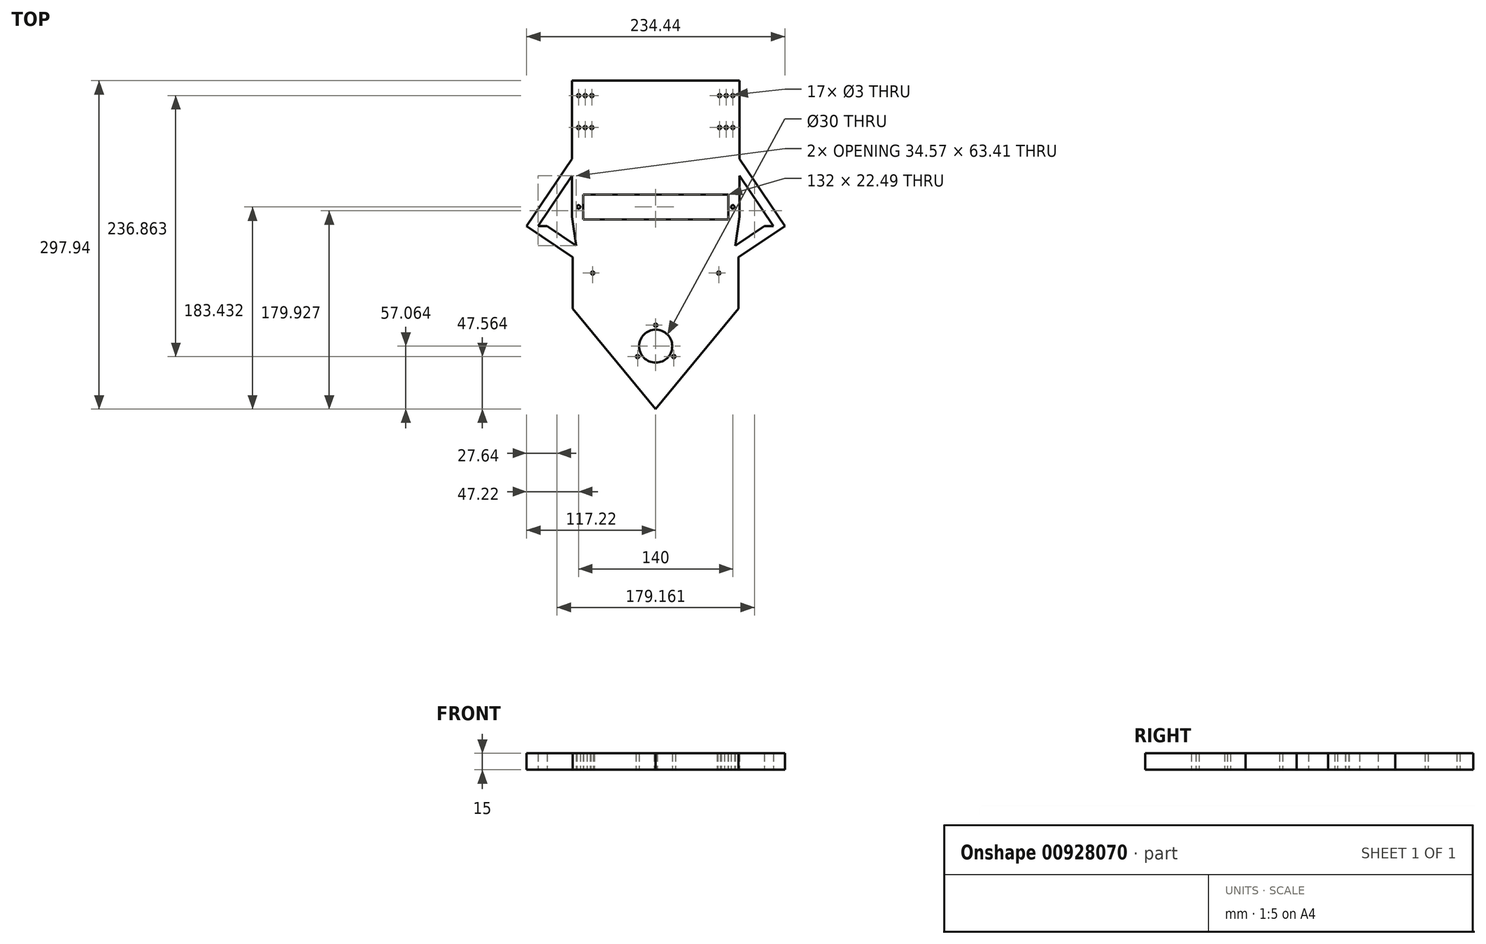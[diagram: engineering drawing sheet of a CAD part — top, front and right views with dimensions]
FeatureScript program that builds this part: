
annotation { "Feature Type Name" : "Feature", "Feature Type Description" : "" }
export const myFeature = defineFeature(function(context is Context, id is Id, definition is map)
    precondition{}
    {
        {
            var Q0;
            Q0=qCreatedBy(makeId("Top.planeOp"),FACE);
            var sketch = newSketch(context, id + "F0", { "sketchPlane" : qUnion([Q0])});
            skLineSegment(sketch, "E0.top", {"start": v(76, 131.87) * mm, "end": v(-76, 131.87) * mm});
            skLineSegment(sketch, "E0.left", {"start": v(76, 8.63) * mm, "end": v(76, 131.87) * mm});
            skLineSegment(sketch, "E0.right", {"start": v(-76, 8.63) * mm, "end": v(-76, 131.87) * mm});
            skPoint(sketch, "E0.middle", {"position": v(0, 70.25) * mm});
            skCircle(sketch, "E1", {"center": v(70, 118.36) * mm, "radius": 1.5 * mm});
            skCircle(sketch, "E2.1.0.0", {"center": v(64, 118.36) * mm, "radius": 1.5 * mm});
            skCircle(sketch, "E2.2.0.0", {"center": v(58, 118.36) * mm, "radius": 1.5 * mm});
            skCircle(sketch, "E3.MirrorC", {"center": v(58, 89.36) * mm, "radius": 1.5 * mm});
            skCircle(sketch, "E4.MirrorC", {"center": v(70, 89.36) * mm, "radius": 1.5 * mm});
            skCircle(sketch, "E5.MirrorC", {"center": v(64, 89.36) * mm, "radius": 1.5 * mm});
            skCircle(sketch, "E6.MirrorC", {"center": v(-58, 118.36) * mm, "radius": 1.5 * mm});
            skCircle(sketch, "E7.MirrorC", {"center": v(-64, 118.36) * mm, "radius": 1.5 * mm});
            skCircle(sketch, "E8.MirrorC", {"center": v(-70, 118.36) * mm, "radius": 1.5 * mm});
            skCircle(sketch, "E9.MirrorC", {"center": v(-58, 89.36) * mm, "radius": 1.5 * mm});
            skCircle(sketch, "E10.MirrorC", {"center": v(-64, 89.36) * mm, "radius": 1.5 * mm});
            skCircle(sketch, "E11.MirrorC", {"center": v(-70, 89.36) * mm, "radius": 1.5 * mm});
            skLineSegment(sketch, "E12", {"start": v(0, 74) * mm, "end": v(0, -73.54) * mm});
            skLineSegment(sketch, "E13", {"start": v(-83.19, 105.86) * mm, "end": v(-83.19, 60.86) * mm});
            skLineSegment(sketch, "E14", {"start": v(-76, 60.86) * mm, "end": v(-117.22, 0) * mm});
            skLineSegment(sketch, "E15", {"start": v(-117.22, 0) * mm, "end": v(-75.22, -28.45) * mm});
            skLineSegment(sketch, "E16", {"start": v(-76, 45.56) * mm, "end": v(-106.87, 0) * mm});
            skLineSegment(sketch, "E17", {"start": v(-104.28, 3.82) * mm, "end": v(-72.3, -17.85) * mm});
            skLineSegment(sketch, "E18", {"start": v(-75.22, -28.45) * mm, "end": v(-75.22, -75.05) * mm});
            skLineSegment(sketch, "E19", {"start": v(-58.47, -47.62) * mm, "end": v(-58.47, -45.58) * mm});
            skLineSegment(sketch, "E20", {"start": v(0, -73.54) * mm, "end": v(0, -166.07) * mm});
            skLineSegment(sketch, "E21", {"start": v(0, -166.07) * mm, "end": v(-75.22, -75.05) * mm});
            skLineSegment(sketch, "E22.MirrorCS", {"start": v(76, 60.86) * mm, "end": v(117.22, 0) * mm});
            skLineSegment(sketch, "E23.MirrorCS", {"start": v(76, 45.56) * mm, "end": v(106.87, 0) * mm});
            skLineSegment(sketch, "E24.MirrorCS", {"start": v(117.22, 0) * mm, "end": v(75.22, -28.45) * mm});
            skLineSegment(sketch, "E25.MirrorCS", {"start": v(104.28, 3.82) * mm, "end": v(72.3, -17.85) * mm});
            skLineSegment(sketch, "E26.MirrorCS", {"start": v(58.47, -47.62) * mm, "end": v(58.47, -45.58) * mm});
            skLineSegment(sketch, "E27.MirrorCS", {"start": v(75.22, -28.45) * mm, "end": v(75.22, -75.05) * mm});
            skLineSegment(sketch, "E28.MirrorCS", {"start": v(0, -166.07) * mm, "end": v(75.22, -75.05) * mm});
            skCircle(sketch, "E29", {"center": v(0, -109) * mm, "radius": 15 * mm});
            skLineSegment(sketch, "E30", {"start": v(117.22, 0) * mm, "end": v(-117.22, 0) * mm});
            skLineSegment(sketch, "E31", {"start": v(87.88, 28.02) * mm, "end": v(83.88, 28.02) * mm});
            skPoint(sketch, "E32.end.orphan", {"position": v(-58.47, -75.05) * mm});
            skPoint(sketch, "E33.MirrorCS.end.orphan", {"position": v(58.47, -75.05) * mm});
            skPoint(sketch, "E33.MirrorCS.start.orphan", {"position": v(75.22, -75.05) * mm});
            skPoint(sketch, "E34.orphan", {"position": v(-64.47, -23.15) * mm});
            skPoint(sketch, "E35.orphan", {"position": v(-83.05, -23.15) * mm});
            skPoint(sketch, "E36.orphan", {"position": v(75.22, -28.45) * mm});
            skPoint(sketch, "E37.orphan", {"position": v(83.05, -23.15) * mm});
            skPoint(sketch, "E38.orphan", {"position": v(111.38, 8.63) * mm});
            skPoint(sketch, "E39.orphan", {"position": v(110.12, -4.81) * mm});
            skPoint(sketch, "E40.orphan", {"position": v(-110.12, -4.81) * mm});
            skPoint(sketch, "E41.orphan", {"position": v(-111.38, 8.63) * mm});
            skPoint(sketch, "E42.orphan", {"position": v(-65.64, 60.86) * mm});
            skPoint(sketch, "E43.orphan", {"position": v(65.64, 60.86) * mm});
            skPoint(sketch, "E44.orphan", {"position": v(64.47, -23.15) * mm});
            skPoint(sketch, "E45.orphan", {"position": v(0, 17.78) * mm});
            skPoint(sketch, "E46.trimOffspring.end.orphan", {"position": v(0, 8.63) * mm});
            skLineSegment(sketch, "E47", {"start": v(-76, 8.63) * mm, "end": v(-72.3, -17.85) * mm});
            skLineSegment(sketch, "E48", {"start": v(76, 8.63) * mm, "end": v(72.3, -17.85) * mm});
            skPoint(sketch, "E49.start.orphan", {"position": v(-58.47, -20.2) * mm});
            skPoint(sketch, "E50.orphan", {"position": v(58.47, -20.2) * mm});
            skCircle(sketch, "E51", {"center": v(0, -109) * mm, "radius": 19 * mm, "construction": true});
            skCircle(sketch, "E52", {"center": v(0, -90) * mm, "radius": 1.5 * mm});
            skCircle(sketch, "E53.1.0", {"center": v(-16.45, -118.5) * mm, "radius": 1.5 * mm});
            skCircle(sketch, "E53.2.0", {"center": v(16.45, -118.5) * mm, "radius": 1.5 * mm});
            skLineSegment(sketch, "E54", {"start": v(146.13, 131.87) * mm, "end": v(146.13, -166.07) * mm});
            skPoint(sketch, "E55.MirrorCS.start.orphan", {"position": v(0, -73.54) * mm});
            skLineSegment(sketch, "E56", {"start": v(70, 118.36) * mm, "end": v(76, 118.36) * mm});
            skSolve(sketch);
        }
        {
            var Q0;
            Q0 = qSketchRegion(id + "F0", true);
            extrude(context, id + "F1", {"entities" : qUnion([Q0]), "depth" : 5 * mm, "offsetDistance" : 25 * mm});
        }
        {
            var Q0;
            Q0 = qSketchRegion(id + "F0", true);
            extrude(context, id + "F2", {"entities" : qUnion([Q0]), "operationType" : NewBodyOperationType.ADD, "depth" : 25 * mm, "offsetDistance" : 25 * mm});
        }
        {
            var Q0;
            Q0 = qSketchRegion(id + "F0", true);
            extrude(context, id + "F3", {"entities" : qUnion([Q0]), "operationType" : NewBodyOperationType.ADD, "depth" : 25 * mm, "offsetDistance" : 25 * mm});
        }
        {
            var Q0;
            Q0=qCreatedBy(makeId("Top.planeOp"),FACE);
            var sketch = newSketch(context, id + "F4", { "sketchPlane" : qUnion([Q0])});
            skPoint(sketch, "E57.orphan", {"position": v(0, -33.88) * mm});
            skPoint(sketch, "E58.start.orphan", {"position": v(66, -40.57) * mm});
            skPoint(sketch, "E59.orphan", {"position": v(70, -40.57) * mm});
            skPoint(sketch, "E60.orphan", {"position": v(-91.32, -47.26) * mm});
            skPoint(sketch, "E61.orphan", {"position": v(91.32, -47.26) * mm});
            skPoint(sketch, "E62.orphan", {"position": v(0, -7.87) * mm});
            skLineSegment(sketch, "E63", {"start": v(-66, 6.12) * mm, "end": v(-66, 28.6) * mm});
            skLineSegment(sketch, "E64", {"start": v(66, 28.6) * mm, "end": v(66, 6.12) * mm});
            skLineSegment(sketch, "E65", {"start": v(-66, 6.12) * mm, "end": v(-49.92, 6.12) * mm});
            skLineSegment(sketch, "E66", {"start": v(-49.92, 6.12) * mm, "end": v(66, 6.12) * mm});
            skLineSegment(sketch, "E67", {"start": v(66, 28.6) * mm, "end": v(-66, 28.6) * mm});
            skPoint(sketch, "E68.orphan", {"position": v(66, 54.65) * mm});
            skPoint(sketch, "E69.top.end.orphan", {"position": v(0, -26.12) * mm});
            skPoint(sketch, "E70.start.orphan", {"position": v(0, -47.26) * mm});
            skPoint(sketch, "E69.left.end.orphan", {"position": v(66, -26.12) * mm});
            skPoint(sketch, "E71.orphan", {"position": v(66, -33.88) * mm});
            skPoint(sketch, "E72.left.end.orphan", {"position": v(66, -47.26) * mm});
            skPoint(sketch, "E73.endSnap0", {"position": v(-66, 17.36) * mm});
            skCircle(sketch, "E74", {"center": v(70, 17.36) * mm, "radius": 1.6 * mm});
            skCircle(sketch, "E75", {"center": v(-70, 17.31) * mm, "radius": 1.6 * mm});
            skLineSegment(sketch, "E76.trimOffspring", {"start": v(-70, 15.71) * mm, "end": v(-70, 17.31) * mm});
            skLineSegment(sketch, "E77.trimOffspring", {"start": v(70, 15.76) * mm, "end": v(70, 17.36) * mm});
            skSolve(sketch);
        }
        {
            var Q0;
            Q0 = qSketchRegion(id + "F4", true);
            extrude(context, id + "F5", {"entities" : qUnion([Q0]), "operationType" : NewBodyOperationType.REMOVE, "depth" : 93 * mm, "offsetDistance" : 25 * mm});
        }
        {
            var Q0;
            Q0 = qSketchRegion(id + "F0", true);
            extrude(context, id + "F6", {"entities" : qUnion([Q0]), "operationType" : NewBodyOperationType.ADD, "depth" : 8 * mm, "offsetDistance" : 25 * mm});
        }
        {
            var Q0;
            Q0=qCreatedBy(makeId("Top.planeOp"),FACE);
            var sketch = newSketch(context, id + "F7", { "sketchPlane" : qUnion([Q0])});
            skPoint(sketch, "E78.orphan", {"position": v(16.9, 9.36) * mm});
            skLineSegment(sketch, "E79", {"start": v(-57.22, -41.16) * mm, "end": v(-57.22, -42.66) * mm});
            skCircle(sketch, "E80", {"center": v(-57.22, -42.66) * mm, "radius": 1.5 * mm});
            skCircle(sketch, "E81.MirrorC", {"center": v(57.22, -42.66) * mm, "radius": 1.5 * mm});
            skPoint(sketch, "E82.end.orphan", {"position": v(16.9, -11.2) * mm});
            skPoint(sketch, "E83.start.orphan", {"position": v(0, -64.76) * mm});
            skLineSegment(sketch, "E84", {"start": v(-57.22, -47.72) * mm, "end": v(58.33, -47.72) * mm});
            skSolve(sketch);
        }
        {
            var Q0;
            Q0 = qSketchRegion(id + "F4", true);
            extrude(context, id + "F8", {"entities" : qUnion([Q0]), "operationType" : NewBodyOperationType.REMOVE, "depth" : 126 * mm, "offsetDistance" : 25 * mm});
        }
        {
            var Q0;
            Q0 = qSketchRegion(id + "F7", true);
            extrude(context, id + "F9", {"entities" : qUnion([Q0]), "operationType" : NewBodyOperationType.REMOVE, "depth" : 51.9 * mm, "offsetDistance" : 25 * mm});
        }
        {
            var Q0;
            Q0 = qSketchRegion(id + "F0", true);
            extrude(context, id + "F10", {"entities" : qUnion([Q0]), "operationType" : NewBodyOperationType.ADD, "depth" : 5 * mm, "offsetDistance" : 25 * mm});
        }
        {
            var Q0;
            Q0=makeQuery(id+"F10.boolean.opBoolean","SPLIT",FACE,{"disambiguationData":[TD([makeQuery(id+"F5.boolean.opBoolean","COPY",FACE,{"derivedFrom":makeQuery(id+"F5.opExtrude","SWEPT_FACE",FACE,{"disambiguationData":[OSD([sQuery(id+"F4.wireOp",EDGE,"E63")])]})})])],"derivedFrom":makeQuery(id+"F10.opExtrude","CAP_FACE",FACE,{"disambiguationData":[OSD([sQuery(id+"F0.wireOp",EDGE,"E0.right"),sQuery(id+"F0.wireOp",EDGE,"E1"),sQuery(id+"F0.wireOp",EDGE,"E2.1.0.0"),sQuery(id+"F0.wireOp",EDGE,"E2.2.0.0"),sQuery(id+"F0.wireOp",EDGE,"E3.MirrorC"),sQuery(id+"F0.wireOp",EDGE,"E4.MirrorC"),sQuery(id+"F0.wireOp",EDGE,"E5.MirrorC"),sQuery(id+"F0.wireOp",EDGE,"E6.MirrorC"),sQuery(id+"F0.wireOp",EDGE,"E7.MirrorC"),sQuery(id+"F0.wireOp",EDGE,"E8.MirrorC"),sQuery(id+"F0.wireOp",EDGE,"E9.MirrorC"),sQuery(id+"F0.wireOp",EDGE,"E10.MirrorC"),sQuery(id+"F0.wireOp",EDGE,"E11.MirrorC"),sQuery(id+"F0.wireOp",EDGE,"E14"),sQuery(id+"F0.wireOp",EDGE,"E15"),sQuery(id+"F0.wireOp",EDGE,"E16"),sQuery(id+"F0.wireOp",EDGE,"E17"),sQuery(id+"F0.wireOp",EDGE,"E18"),sQuery(id+"F0.wireOp",EDGE,"E19"),sQuery(id+"F0.wireOp",EDGE,"E21"),sQuery(id+"F0.wireOp",EDGE,"hH9Nh53m-2MCM-Tzpd-290s-laI18iUmR80W"),sQuery(id+"F0.wireOp",EDGE,"E22.MirrorCS"),sQuery(id+"F0.wireOp",EDGE,"E0.left"),sQuery(id+"F0.wireOp",EDGE,"E23.MirrorCS"),sQuery(id+"F0.wireOp",EDGE,"E24.MirrorCS"),sQuery(id+"F0.wireOp",EDGE,"E25.MirrorCS"),sQuery(id+"F0.wireOp",EDGE,"E26.MirrorCS"),sQuery(id+"F0.wireOp",EDGE,"E27.MirrorCS"),sQuery(id+"F0.wireOp",EDGE,"E55.MirrorCS"),sQuery(id+"F0.wireOp",EDGE,"E28.MirrorCS"),sQuery(id+"F0.wireOp",EDGE,"ywcaavka-473P-WrbY-odvZ-nprz8qSF7bsu"),sQuery(id+"F0.wireOp",EDGE,"E29"),sQuery(id+"F0.wireOp",EDGE,"E30"),sQuery(id+"F0.wireOp",EDGE,"E47"),sQuery(id+"F0.wireOp",EDGE,"E48"),sQuery(id+"F0.wireOp",EDGE,"UQelqqcz-CsA3-FEmt-8LGz-mbn3CGqxLyQe")])],"isStart":false})});
            extrude(context, id + "F11", {"entities" : qUnion([Q0]), "operationType" : NewBodyOperationType.REMOVE, "oppositeDirection" : true, "depth" : 123 * mm, "offsetDistance" : 25 * mm});
        }
        {
            var Q0;
            {var subQ0=sQuery(id+"F0.wireOp",EDGE,"UQelqqcz-CsA3-FEmt-8LGz-mbn3CGqxLyQe");var subQ1=sQuery(id+"F0.wireOp",EDGE,"E48");var subQ2=sQuery(id+"F0.wireOp",EDGE,"E47");var subQ3=sQuery(id+"F0.wireOp",EDGE,"E30");var subQ4=sQuery(id+"F0.wireOp",EDGE,"E29");var subQ5=sQuery(id+"F0.wireOp",EDGE,"ywcaavka-473P-WrbY-odvZ-nprz8qSF7bsu");var subQ6=sQuery(id+"F0.wireOp",EDGE,"E28.MirrorCS");var subQ7=sQuery(id+"F0.wireOp",EDGE,"E55.MirrorCS");var subQ8=sQuery(id+"F0.wireOp",EDGE,"E27.MirrorCS");var subQ9=sQuery(id+"F0.wireOp",EDGE,"E26.MirrorCS");var subQ10=sQuery(id+"F0.wireOp",EDGE,"E25.MirrorCS");var subQ11=sQuery(id+"F0.wireOp",EDGE,"E24.MirrorCS");var subQ12=sQuery(id+"F0.wireOp",EDGE,"E23.MirrorCS");var subQ13=sQuery(id+"F0.wireOp",EDGE,"E0.left");var subQ14=sQuery(id+"F0.wireOp",EDGE,"E22.MirrorCS");var subQ15=sQuery(id+"F0.wireOp",EDGE,"hH9Nh53m-2MCM-Tzpd-290s-laI18iUmR80W");var subQ16=sQuery(id+"F0.wireOp",EDGE,"E21");var subQ17=sQuery(id+"F0.wireOp",EDGE,"E19");var subQ18=sQuery(id+"F0.wireOp",EDGE,"E18");var subQ19=sQuery(id+"F0.wireOp",EDGE,"E17");var subQ20=sQuery(id+"F0.wireOp",EDGE,"E16");var subQ21=sQuery(id+"F0.wireOp",EDGE,"E15");var subQ22=sQuery(id+"F0.wireOp",EDGE,"E14");var subQ23=sQuery(id+"F0.wireOp",EDGE,"E11.MirrorC");var subQ24=sQuery(id+"F0.wireOp",EDGE,"E10.MirrorC");var subQ25=sQuery(id+"F0.wireOp",EDGE,"E9.MirrorC");var subQ26=sQuery(id+"F0.wireOp",EDGE,"E8.MirrorC");var subQ27=sQuery(id+"F0.wireOp",EDGE,"E7.MirrorC");var subQ28=sQuery(id+"F0.wireOp",EDGE,"E6.MirrorC");var subQ29=sQuery(id+"F0.wireOp",EDGE,"E5.MirrorC");var subQ30=sQuery(id+"F0.wireOp",EDGE,"E4.MirrorC");var subQ31=sQuery(id+"F0.wireOp",EDGE,"E3.MirrorC");var subQ32=sQuery(id+"F0.wireOp",EDGE,"E2.2.0.0");var subQ33=sQuery(id+"F0.wireOp",EDGE,"E2.1.0.0");var subQ34=sQuery(id+"F0.wireOp",EDGE,"E1");var subQ35=sQuery(id+"F0.wireOp",EDGE,"E0.right");Q0=makeQuery(id+"F10.boolean.opBoolean","MERGE",FACE,{"derivedFrom":[makeQuery(id+"F6.boolean.opBoolean","MERGE",FACE,{"derivedFrom":[makeQuery(id+"F1.opExtrude","CAP_FACE",FACE,{"disambiguationData":[OSD([subQ35,subQ34,subQ33,subQ32,subQ31,subQ30,subQ29,subQ28,subQ27,subQ26,subQ25,subQ24,subQ23,subQ22,subQ21,subQ20,subQ19,subQ18,subQ17,subQ16,subQ15,subQ14,subQ13,subQ12,subQ11,subQ10,subQ9,subQ8,subQ7,subQ6,subQ5,subQ4,subQ3,subQ2,subQ1,subQ0])],"isStart":true}),makeQuery(id+"F6.opExtrude","CAP_FACE",FACE,{"disambiguationData":[OSD([subQ35,subQ34,subQ33,subQ32,subQ31,subQ30,subQ29,subQ28,subQ27,subQ26,subQ25,subQ24,subQ23,subQ22,subQ21,subQ20,subQ19,subQ18,subQ17,subQ16,subQ15,subQ14,subQ13,subQ12,subQ11,subQ10,subQ9,subQ8,subQ7,subQ6,subQ5,subQ4,subQ3,subQ2,subQ1,subQ0])],"isStart":true})]}),makeQuery(id+"F10.opExtrude","CAP_FACE",FACE,{"disambiguationData":[OSD([subQ35,subQ34,subQ33,subQ32,subQ31,subQ30,subQ29,subQ28,subQ27,subQ26,subQ25,subQ24,subQ23,subQ22,subQ21,subQ20,subQ19,subQ18,subQ17,subQ16,subQ15,subQ14,subQ13,subQ12,subQ11,subQ10,subQ9,subQ8,subQ7,subQ6,subQ5,subQ4,subQ3,subQ2,subQ1,subQ0])],"isStart":true})]});}
            extrude(context, id + "F12", {"entities" : qUnion([Q0]), "operationType" : NewBodyOperationType.REMOVE, "oppositeDirection" : true, "depth" : 10 * mm, "offsetDistance" : 25 * mm});
        }
    });
